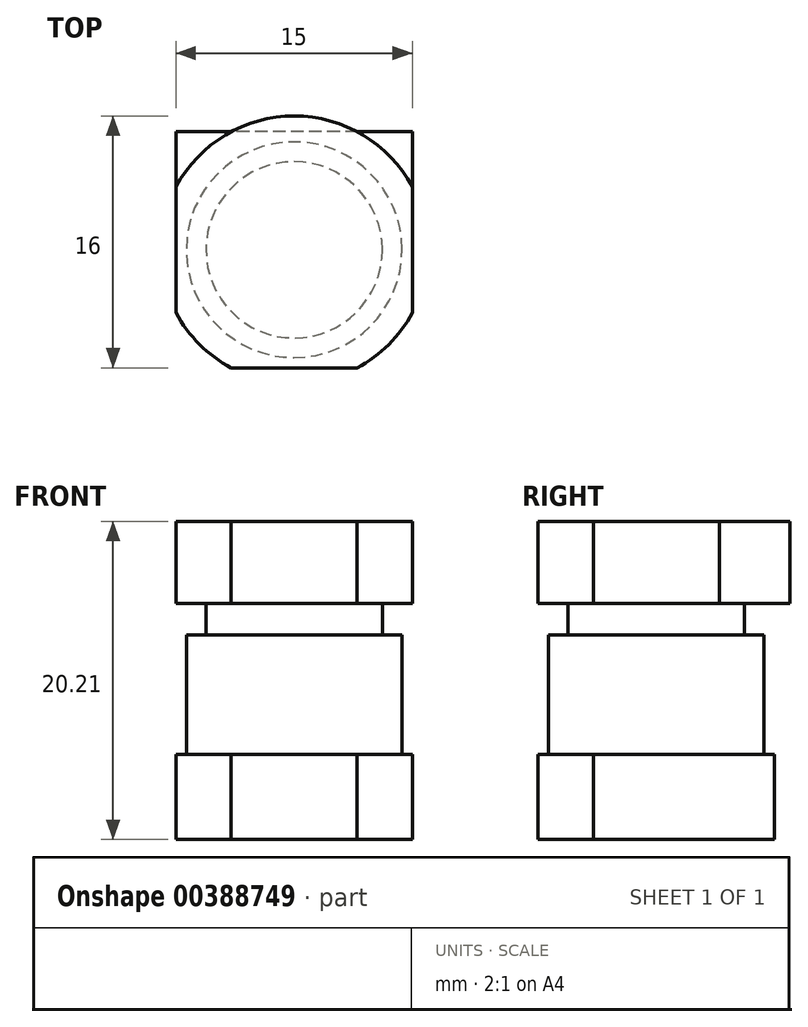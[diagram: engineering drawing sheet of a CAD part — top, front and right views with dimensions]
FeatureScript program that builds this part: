
annotation { "Feature Type Name" : "Feature", "Feature Type Description" : "" }
export const myFeature = defineFeature(function(context is Context, id is Id, definition is map)
    precondition{}
    {
        {
            var Q0;
            Q0=qCreatedBy(makeId("Top.planeOp"),FACE);
            var sketch = newSketch(context, id + "F0", { "sketchPlane" : qUnion([Q0])});
            skCircle(sketch, "E0", {"center": v(0, 0) * mm, "radius": 8.5 * mm});
            skCircle(sketch, "E1", {"center": v(0, 0) * mm, "radius": 5.6 * mm});
            skCircle(sketch, "E2", {"center": v(0, 0) * mm, "radius": 6.85 * mm});
            skLineSegment(sketch, "E3.bottom", {"start": v(7.5, -7.5) * mm, "end": v(-7.5, -7.5) * mm});
            skLineSegment(sketch, "E3.top", {"start": v(7.5, 7.5) * mm, "end": v(-7.5, 7.5) * mm});
            skLineSegment(sketch, "E3.left", {"start": v(7.5, -7.5) * mm, "end": v(7.5, 7.5) * mm});
            skLineSegment(sketch, "E3.right", {"start": v(-7.5, -7.5) * mm, "end": v(-7.5, 7.5) * mm});
            skSolve(sketch);
        }
        {
            var Q0;
            {var subQ0=sQuery(id+"F0.wireOp",EDGE,"E3.top");var subQ1=sQuery(id+"F0.wireOp",EDGE,"E0");var subQ2=makeQuery(id+"F0.imprint","INTERSECT",VERTEX,{"disambiguationData":[OD(0.0)],"derivedFrom":[subQ1,subQ0]});Q0=makeQuery(id+"F0.imprint","IMPRINT",FACE,{"disambiguationData":[TD([[makeQuery(id+"F0.imprint","IMPRINT",EDGE,{"disambiguationData":[TD([[subQ2,1.0]])],"derivedFrom":subQ1}),-1.0]])]});}
            var Q1;
            Q1=makeQuery(id+"F0.imprint","IMPRINT",FACE,{"disambiguationData":[TD([[makeQuery(id+"F0.imprint","IMPRINT",EDGE,{"derivedFrom":sQuery(id+"F0.wireOp",EDGE,"E2")}),-1.0]])]});
            var Q2;
            Q2=makeQuery(id+"F0.imprint","IMPRINT",FACE,{"disambiguationData":[TD([[makeQuery(id+"F0.imprint","IMPRINT",EDGE,{"derivedFrom":sQuery(id+"F0.wireOp",EDGE,"E1")}),-1.0]])]});
            var Q3;
            Q3=makeQuery(id+"F0.imprint","IMPRINT",FACE,{"disambiguationData":[TD([[makeQuery(id+"F0.imprint","IMPRINT",EDGE,{"derivedFrom":sQuery(id+"F0.wireOp",EDGE,"E1")}),1.0]])]});
            var Q4;
            {var subQ0=sQuery(id+"F0.wireOp",EDGE,"E3.top");var subQ1=sQuery(id+"F0.wireOp",EDGE,"E0");var subQ2=makeQuery(id+"F0.imprint","INTERSECT",VERTEX,{"disambiguationData":[OD(1.0)],"derivedFrom":[subQ1,subQ0]});Q4=makeQuery(id+"F0.imprint","IMPRINT",FACE,{"disambiguationData":[TD([[makeQuery(id+"F0.imprint","IMPRINT",EDGE,{"disambiguationData":[TD([[subQ2,-1.0]])],"derivedFrom":subQ1}),-1.0]])]});}
            var Q5;
            {var subQ0=sQuery(id+"F0.wireOp",EDGE,"E3.right");var subQ1=sQuery(id+"F0.wireOp",EDGE,"E0");var subQ2=makeQuery(id+"F0.imprint","INTERSECT",VERTEX,{"disambiguationData":[OD(1.0)],"derivedFrom":[subQ1,subQ0]});Q5=makeQuery(id+"F0.imprint","IMPRINT",FACE,{"disambiguationData":[TD([[makeQuery(id+"F0.imprint","IMPRINT",EDGE,{"disambiguationData":[TD([[subQ2,-1.0]])],"derivedFrom":subQ1}),-1.0]])]});}
            var Q6;
            {var subQ0=sQuery(id+"F0.wireOp",EDGE,"E3.bottom");var subQ1=sQuery(id+"F0.wireOp",EDGE,"E0");var subQ2=makeQuery(id+"F0.imprint","INTERSECT",VERTEX,{"disambiguationData":[OD(1.0)],"derivedFrom":[subQ1,subQ0]});Q6=makeQuery(id+"F0.imprint","IMPRINT",FACE,{"disambiguationData":[TD([[makeQuery(id+"F0.imprint","IMPRINT",EDGE,{"disambiguationData":[TD([[subQ2,-1.0]])],"derivedFrom":subQ1}),-1.0]])]});}
            extrude(context, id + "F1", {"entities" : qUnion([Q0, Q1, Q2, Q3, Q4, Q5, Q6]), "depth" : 5.4 * mm});
        }
        {
            var Q0;
            Q0=makeQuery(id+"F0.imprint","IMPRINT",FACE,{"disambiguationData":[TD([[makeQuery(id+"F0.imprint","IMPRINT",EDGE,{"derivedFrom":sQuery(id+"F0.wireOp",EDGE,"E1")}),1.0]])]});
            var Q1;
            Q1=makeQuery(id+"F0.imprint","IMPRINT",FACE,{"disambiguationData":[TD([[makeQuery(id+"F0.imprint","IMPRINT",EDGE,{"derivedFrom":sQuery(id+"F0.wireOp",EDGE,"E1")}),-1.0]])]});
            extrude(context, id + "F2", {"entities" : qUnion([Q0, Q1]), "operationType" : NewBodyOperationType.ADD, "depth" : 13 * mm});
        }
        {
            var Q0;
            Q0=makeQuery(id+"F0.imprint","IMPRINT",FACE,{"disambiguationData":[TD([[makeQuery(id+"F0.imprint","IMPRINT",EDGE,{"derivedFrom":sQuery(id+"F0.wireOp",EDGE,"E1")}),1.0]])]});
            extrude(context, id + "F3", {"entities" : qUnion([Q0]), "operationType" : NewBodyOperationType.ADD, "depth" : 15 * mm});
        }
        {
            var Q0;
            {var subQ0=sQuery(id+"F0.wireOp",EDGE,"E3.right");var subQ1=sQuery(id+"F0.wireOp",EDGE,"E0");var subQ2=makeQuery(id+"F0.imprint","INTERSECT",VERTEX,{"disambiguationData":[OD(0.0)],"derivedFrom":[subQ1,subQ0]});Q0=makeQuery(id+"F0.imprint","IMPRINT",FACE,{"disambiguationData":[TD([[makeQuery(id+"F0.imprint","IMPRINT",EDGE,{"disambiguationData":[TD([[subQ2,-1.0]])],"derivedFrom":subQ1}),1.0]])]});}
            var Q1;
            Q1=makeQuery(id+"F0.imprint","IMPRINT",FACE,{"disambiguationData":[TD([[makeQuery(id+"F0.imprint","IMPRINT",EDGE,{"derivedFrom":sQuery(id+"F0.wireOp",EDGE,"E2")}),-1.0]])]});
            var Q2;
            Q2=makeQuery(id+"F0.imprint","IMPRINT",FACE,{"disambiguationData":[TD([[makeQuery(id+"F0.imprint","IMPRINT",EDGE,{"derivedFrom":sQuery(id+"F0.wireOp",EDGE,"E1")}),-1.0]])]});
            var Q3;
            Q3=makeQuery(id+"F0.imprint","IMPRINT",FACE,{"disambiguationData":[TD([[makeQuery(id+"F0.imprint","IMPRINT",EDGE,{"derivedFrom":sQuery(id+"F0.wireOp",EDGE,"E1")}),1.0]])]});
            var Q4;
            {var subQ0=sQuery(id+"F0.wireOp",EDGE,"E3.bottom");var subQ1=sQuery(id+"F0.wireOp",EDGE,"E0");var subQ2=makeQuery(id+"F0.imprint","INTERSECT",VERTEX,{"disambiguationData":[OD(0.0)],"derivedFrom":[subQ1,subQ0]});Q4=makeQuery(id+"F0.imprint","IMPRINT",FACE,{"disambiguationData":[TD([[makeQuery(id+"F0.imprint","IMPRINT",EDGE,{"disambiguationData":[TD([[subQ2,-1.0]])],"derivedFrom":subQ1}),1.0]])]});}
            var Q5;
            {var subQ0=sQuery(id+"F0.wireOp",EDGE,"E3.left");var subQ1=sQuery(id+"F0.wireOp",EDGE,"E0");var subQ2=makeQuery(id+"F0.imprint","INTERSECT",VERTEX,{"disambiguationData":[OD(0.0)],"derivedFrom":[subQ1,subQ0]});Q5=makeQuery(id+"F0.imprint","IMPRINT",FACE,{"disambiguationData":[TD([[makeQuery(id+"F0.imprint","IMPRINT",EDGE,{"disambiguationData":[TD([[subQ2,1.0]])],"derivedFrom":subQ1}),1.0]])]});}
            var Q6;
            {var subQ0=sQuery(id+"F0.wireOp",EDGE,"E3.top");var subQ1=sQuery(id+"F0.wireOp",EDGE,"E0");var subQ2=makeQuery(id+"F0.imprint","INTERSECT",VERTEX,{"disambiguationData":[OD(0.0)],"derivedFrom":[subQ1,subQ0]});Q6=makeQuery(id+"F0.imprint","IMPRINT",FACE,{"disambiguationData":[TD([[makeQuery(id+"F0.imprint","IMPRINT",EDGE,{"disambiguationData":[TD([[subQ2,-1.0]])],"derivedFrom":subQ1}),1.0]])]});}
            extrude(context, id + "F4", {"entities" : qUnion([Q0, Q1, Q2, Q3, Q4, Q5, Q6]), "operationType" : NewBodyOperationType.ADD, "depth" : 20.21 * mm, "hasSecondDirection" : true, "secondDirectionOppositeDirection" : false, "secondDirectionDepth" : 15 * mm});
        }
    });
